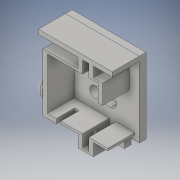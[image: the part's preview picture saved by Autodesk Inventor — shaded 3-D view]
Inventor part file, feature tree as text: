
AUTODESK INVENTOR PART (.ipt)
format: ipt  version: 2016 (Build 200138000, 138)  size: 444,416 bytes
history: native  units: in
note: dims shown in document units (in); Inventor stores cm internally (conversion verified against a paired STEP export)
features: sketch x14, extrude x12, plane x5, fillet x4, hole x2
ambient origin geometry x8: Origin, YZ Plane, XZ Plane, XY Plane, X Axis, Y Axis, Z Axis, Center Point
bodies: Solid1 (feature_tree)
feature tree (37):
  extrude  "Extrusion1"  Depth=0.1181in
  sketch  "Sketch12"  dims[d11=0.0787in d12=0.0787in d13=0.0787in d14=0.0787in d82=0.9016in d83=0.8858in]
  plane  "Work Plane6"
  extrude  "Extrusion5"  Depth=0.9016in
  plane  "Work Plane5"
  hole  "Hole3"  [1 undecoded]
  plane  "Work Plane1"
  extrude  "Extrusion6"  Depth=0.6142in
  extrude  "Extrusion7"  Depth=0.1614in
  plane  "Work Plane4"
  extrude  "Extrusion8"  Depth=0.2992in
  fillet  "Fillet15"  Radius=0.2165in
  plane  "Work Plane3"
  extrude  "Extrusion10"  Depth=0.0787in
  extrude  "Extrusion12"  Depth=0.0787in
  extrude  "Extrusion13"  Depth=0.0787in
  hole  "Hole4"  [1 undecoded]
  extrude  "Extrusion14"  Depth=0.0394in
  extrude  "Extrusion15"  Depth=0.0394in
  extrude  "Extrusion18"  Depth=0.0394in
  fillet  "Fillet38"  Radius=0.0787in
  fillet  "Fillet39"  Radius=0.0394in
  fillet  "Fillet40"  Radius=0.9016in
  extrude  "Extrusion20"  Depth=0.0394in
  sketch  "Sketch1"  dims[d2=0.1181in d3=0.0in d6=0.8976in d9=0.357in d10=0.7139in]
  sketch  "Sketch14"  dims[d85=0.1102in d86=0.1102in]
  sketch  "Sketch17"  dims[d87=0.6142in d88=0.6142in]
  sketch  "Sketch18"  dims[d89=0.1614in d90=0.1614in]
  sketch  "Sketch22"  dims[d91=0.2992in d92=0.2165in d93=0.2165in]
  sketch  "Sketch24"  dims[d95=0.9016in d97=0.0787in]
  sketch  "Sketch30"  dims[d98=0.0787in d100=0.0787in]
  sketch  "Sketch32"  dims[d101=0.0787in d102=0.0787in]
  sketch  "Sketch33"  dims[d103=0.1693in d105=0.0787in]
  sketch  "Sketch35"  dims[d106=0.0394in d107=0.0394in]
  sketch  "Sketch36"  dims[d108=0.0394in d109=0.0394in]
  sketch  "Sketch41"  dims[d110=0.1575in d111=0.0787in d112=0.0787in d113=0.0394in d114=0.9016in]
  sketch  "Sketch43"  dims[d125=0.1378in d130=0.185in d132=0.3543in d133=0.2165in d136=0.0787in d137=0.315in d138=0.0in d139=0.0394in d144=0.0394in d145=0.7461in d146=0.0394in d147=0.07in d148=0.2362in d149=0.119in d150=0.0787in d151=0.5635in d152=0.315in d153=0.8108in d156=0.2717in d157=0.2323in d158=0.2835in d159=0.4016in d160=0.1575in d161=0.0in d164=0.3937in d165=0.0in d166=0.0787in d167=0.0in d171=0.0669in d177=0.0906in d178=0.0in d181=0.0787in d182=0.0787in d185=0.1772in d186=0.0483in d187=0.1063in d188=0.4724in d189=0.0in d190=0.3135in d191=0.4724in d192=0.0in d194=0.2559in d195=0.0394in d196=0.2559in d197=0.0394in d198=0.0787in d199=0.2362in d200=0.1575in d201=0.0787in d202=90.0deg d203=0.315in d204=0.8108in d205=0.1575in d206=0.0in d207=0.0394in d208=0.3937in d209=0.0in d252=0.0197in d253=0.0in d259=0.0512in d260=0.0512in d261=0.0512in d267=0.1969in d268=0.1969in d269=0.1575in d270=0.1575in d271=0.3937in d272=0.0in d26=0.0394in d27=0.0394in]
note: 2 required parameter values undecoded (feature->parameter linkage not recoverable at this tier; creation-order binding heuristic only, values carry confidence <= 0.55)
